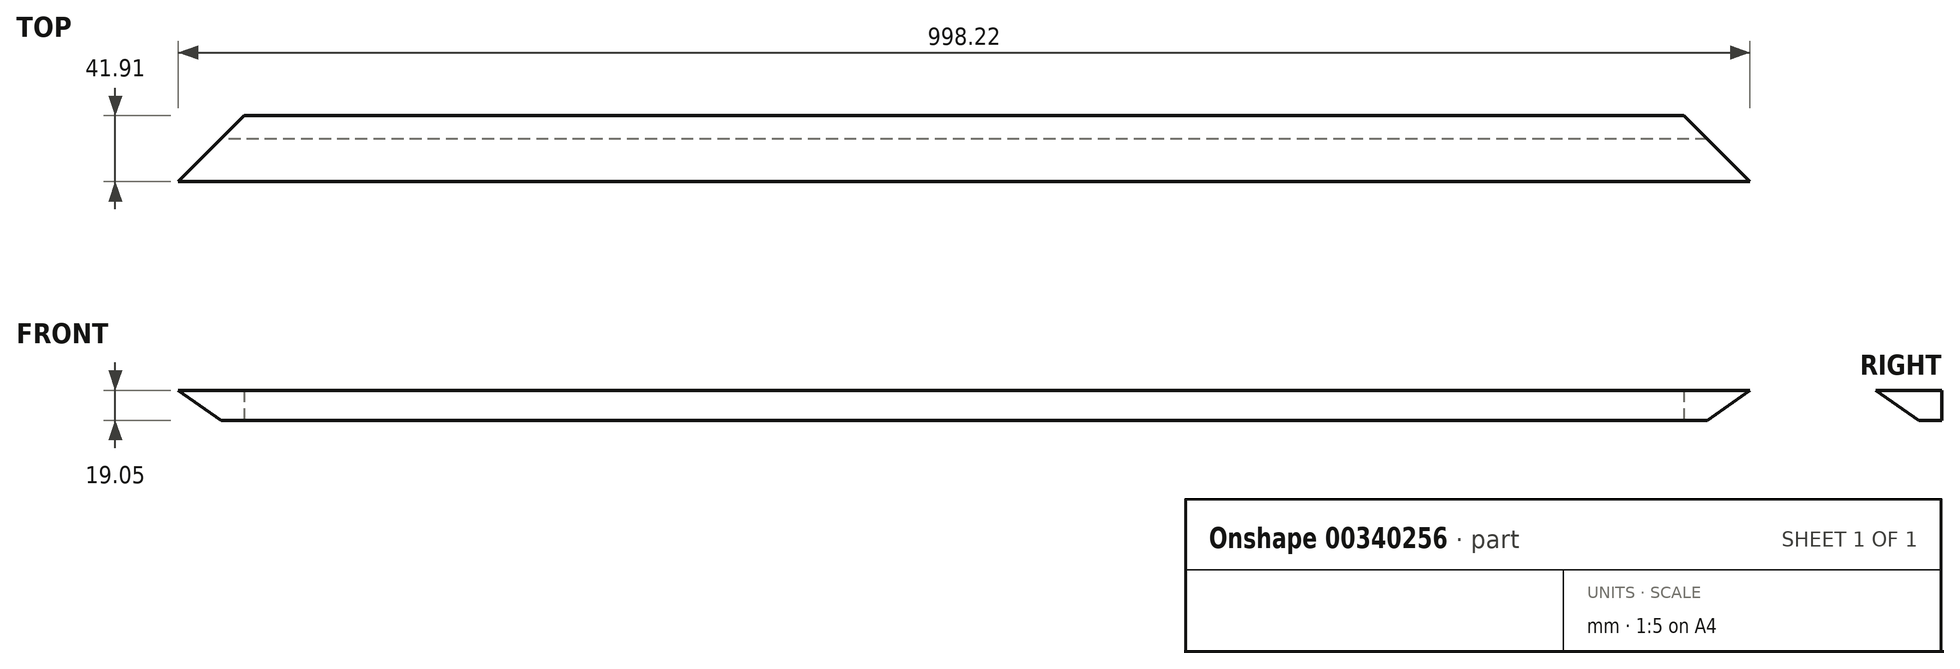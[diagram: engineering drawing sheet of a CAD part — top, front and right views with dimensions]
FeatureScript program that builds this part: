
annotation { "Feature Type Name" : "Feature", "Feature Type Description" : "" }
export const myFeature = defineFeature(function(context is Context, id is Id, definition is map)
    precondition{}
    {
        {
            var Q0;
            Q0=qCreatedBy(makeId("Right.planeOp"),FACE);
            var sketch = newSketch(context, id + "F0", { "sketchPlane" : qUnion([Q0])});
            skLineSegment(sketch, "E0.bottom", {"start": v(0, 19.05) * mm, "end": v(-41.91, 19.05) * mm});
            skLineSegment(sketch, "E0.top", {"start": v(0, 0) * mm, "end": v(-14.7, 0) * mm});
            skLineSegment(sketch, "E0.left", {"start": v(0, 19.05) * mm, "end": v(0, 0) * mm});
            skPoint(sketch, "E0.middle", {"position": v(0, 0) * mm});
            skLineSegment(sketch, "E1", {"start": v(-41.91, 19.05) * mm, "end": v(-14.7, 0) * mm});
            skSolve(sketch);
        }
        {
            var Q0;
            Q0 = qSketchRegion(id + "F0", true);
            extrude(context, id + "F1", {"entities" : qUnion([Q0]), "depth" : 508 * mm, "hasSecondDirection" : true, "secondDirectionOppositeDirection" : true, "secondDirectionDepth" : 508 * mm});
        }
        {
            var Q0;
            Q0=qCreatedBy(makeId("Top.planeOp"),FACE);
            var sketch = newSketch(context, id + "F2", { "sketchPlane" : qUnion([Q0])});
            skLineSegment(sketch, "E2", {"start": v(-457.2, 0) * mm, "end": v(457.2, 0) * mm, "construction": true});
            skLineSegment(sketch, "E3", {"start": v(0, 0) * mm, "end": v(0, -153.4) * mm, "construction": true});
            skLineSegment(sketch, "E4", {"start": v(457.2, 0) * mm, "end": v(509.68, 0) * mm});
            skLineSegment(sketch, "E5", {"start": v(509.68, 0) * mm, "end": v(509.68, -52.48) * mm});
            skLineSegment(sketch, "E6", {"start": v(509.68, -52.48) * mm, "end": v(457.2, 0) * mm});
            skLineSegment(sketch, "E7.MirrorCS", {"start": v(-457.2, 0) * mm, "end": v(-509.68, 0) * mm});
            skLineSegment(sketch, "E8.MirrorCS", {"start": v(-509.68, 0) * mm, "end": v(-509.68, -52.48) * mm});
            skLineSegment(sketch, "E9.MirrorCS", {"start": v(-509.68, -52.48) * mm, "end": v(-457.2, 0) * mm});
            skSolve(sketch);
        }
        {
            var Q0;
            Q0 = qSketchRegion(id + "F2", true);
            extrude(context, id + "F3", {"entities" : qUnion([Q0]), "operationType" : NewBodyOperationType.REMOVE, "endBound" : BoundingType.THROUGH_ALL, "depth" : 25.4 * mm});
        }
    });
